# Revit family: ASSAN_1000W_Prefabricated_0,5-0,4_T
name_source: partatom
category: Curtain Panels
units: mm (PartAtom-declared; Revit-internal decimal feet)

## family parameters
Always vertical = Yes
Cut with Voids When Loaded = No
OmniClass Number = 23.25.20.14.11.11.17
OmniClass Title = Infill Panels
Shared = No

## types (2) — shared parameters
BIMobject category = Insulated panel
Closed cell ratio (EN 14509) = 0,95
Construction Type = 1000_W_Prefabricated
Date of publishing = 001
Design country = ISTANBUL
Dimensional Stability (EN 13165) = Level DS (TH) 11
External Colour = RAL 5010
External Metal Thickness = 0.3
Finish = ASSAN IPN
Flammability Class (EN 13501) = B. S2 . d0
Heat Transmission Coefficient λ (EN 13165) (W/Mk) = 0,022-0,024
Hot Dip Coating Quantity(EN 10327) (gr/m2) = Z70
IFC Classification = Building Element
Installation instructions = https://www.assanpanel.com.tr
Insulation Core Material = Assan PUR
Internal  Metal Thickness = 0.3
Internal Colour = RAL 6050
Manufacturer = Assan Panel San. ve Tic. A.Ş.
Manufacturer country = TURKEY
Manufacturer name = Assan Panel San. ve Tic. A.Ş.
Metal Sheet Type = Galvanized
Model name = ASSAN_1000_W-Prefabricated
NBS Reference Code = 60-88-84
NBS Reference Description = Insulated Wall
Painted Type = Plastisol
Panel orientation = Wall-  panel vertical
Polyurethane Density (EN 1602  (kg/m3) = 40 (±2)
Product certification = https://www.assanpanel.com.tr
Product data url = https://www.assanpanel.com.tr
Product family = Wall Panel
Product group = Insulated Panels
Production Site = İstanbul-İskenderun
QR code = https://www.assanpanel.com.tr
Ral Code = All colors available.Please enter the desired color code

@  :  7032
Region = ALL
Technical description = https://www.assanpanel.com.tr
Temperature Resistance = -200 /+110 ºC
Type Comments = Prepainted Galvanized Steel Structure
URL = https://www.assanpanel.com.tr
Uniclass 2.0 Code = Pr_20_93_85_84
Uniclass 2.0 Description = Structural insulated wall panels
Uniclass 2015 Code = Pr_20_93_85_84
Uniclass 2015 Name = Structural insulated wall panels
Vapor Diffusion Resistance (EN 12086) = 30-100
Version number = Assan_1000_W_Prefabricated
Water absorption (EN ISO 354) = By Volume 2%  (168 hours)
maximum size (m) = Depends on shipping conditions
minimum size  (m) = 3
width  (mm) = 1000-1149

## per-type parameters (varying)
| type | Thicknes |
| ASSAN_1000W_Prefabricated_0,5-0,4_T40 | 40 mm  [stored 0.131234 ft] |
| ASSAN_1000W_Prefabricated_0,5-0,4_T50 | 50 mm  [stored 0.164042 ft] |

note: [stored X ft] marks values corroborated as IEEE doubles in the binary element streams (Revit-internal decimal feet)

## geometry (parser evidence)
native form markers: Sweep x101
no freeform markers — native parametric forms only
